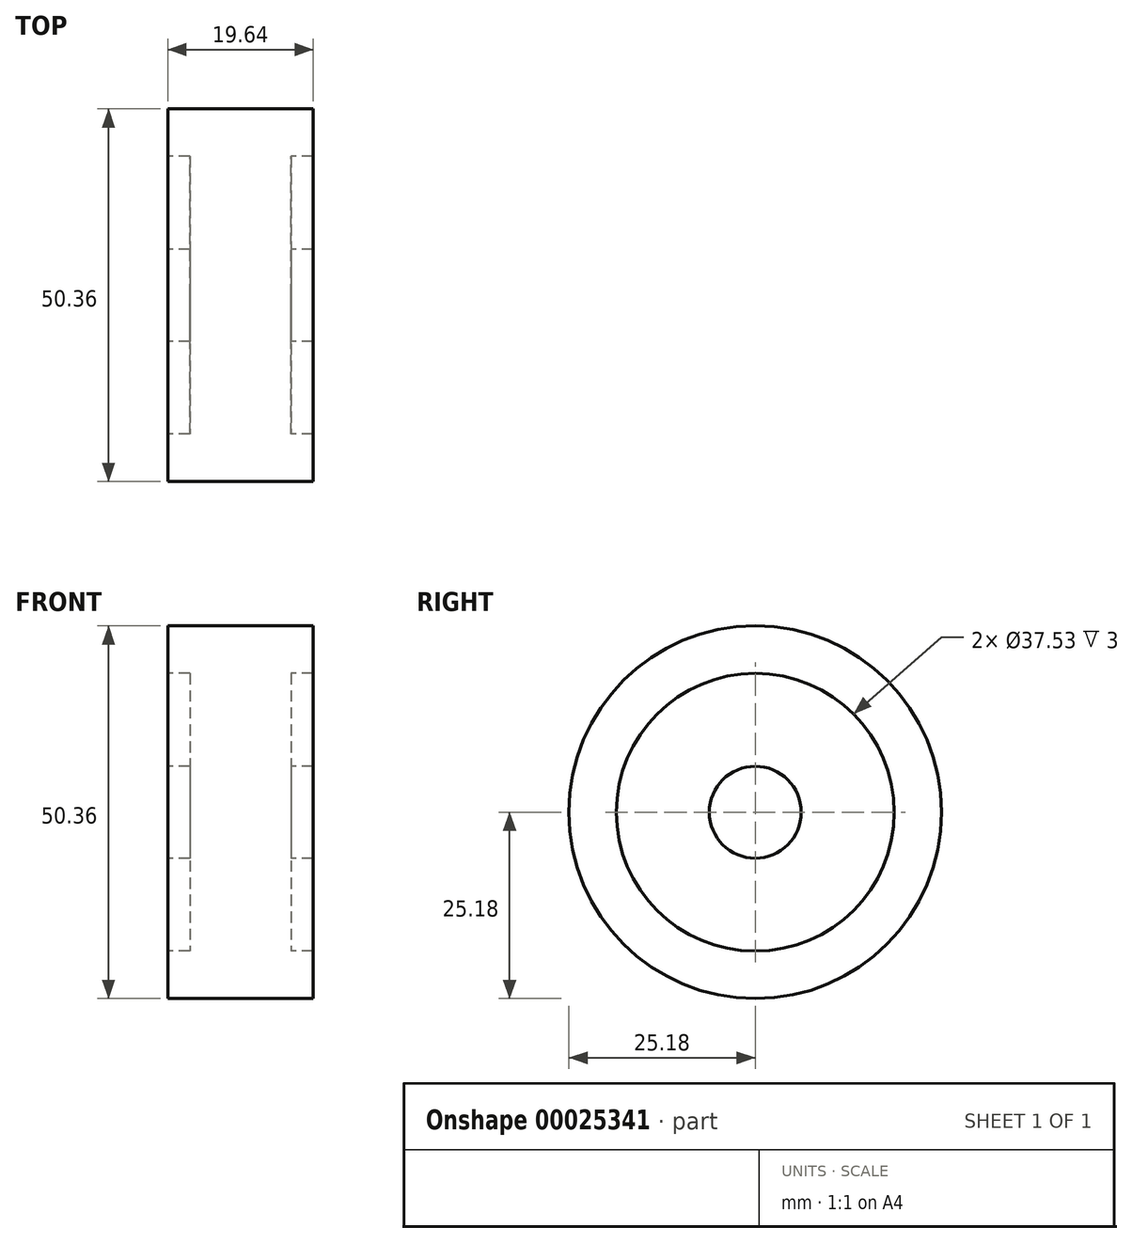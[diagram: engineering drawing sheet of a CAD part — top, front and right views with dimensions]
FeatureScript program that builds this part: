
annotation { "Feature Type Name" : "Feature", "Feature Type Description" : "" }
export const myFeature = defineFeature(function(context is Context, id is Id, definition is map)
    precondition{}
    {
        {
            var Q0;
            Q0=qCreatedBy(makeId("Front.planeOp"),FACE);
            var sketch = newSketch(context, id + "F0", { "sketchPlane" : qUnion([Q0])});
            skLineSegment(sketch, "E0", {"start": v(-18.7, 0) * mm, "end": v(23.1, 0) * mm, "construction": true});
            skLineSegment(sketch, "E1", {"start": v(0, 0) * mm, "end": v(0, 6.21) * mm});
            skLineSegment(sketch, "E2", {"start": v(0, 6.21) * mm, "end": v(-3, 6.21) * mm});
            skLineSegment(sketch, "E3", {"start": v(-3, 6.21) * mm, "end": v(-3, 18.77) * mm});
            skLineSegment(sketch, "E4", {"start": v(-3, 18.77) * mm, "end": v(0, 18.77) * mm});
            skLineSegment(sketch, "E5", {"start": v(0, 18.77) * mm, "end": v(0, 25.18) * mm});
            skLineSegment(sketch, "E6", {"start": v(0, 25.18) * mm, "end": v(-19.64, 25.18) * mm});
            skLineSegment(sketch, "E7", {"start": v(-19.64, 25.18) * mm, "end": v(-19.64, 18.77) * mm});
            skLineSegment(sketch, "E8", {"start": v(-19.64, 18.77) * mm, "end": v(-16.64, 18.77) * mm});
            skLineSegment(sketch, "E9", {"start": v(-16.64, 18.77) * mm, "end": v(-16.64, 6.21) * mm});
            skLineSegment(sketch, "E10", {"start": v(-16.64, 6.21) * mm, "end": v(-19.64, 6.21) * mm});
            skLineSegment(sketch, "E11", {"start": v(-19.64, 6.21) * mm, "end": v(-19.64, 0) * mm});
            skLineSegment(sketch, "E12", {"start": v(-19.64, 0) * mm, "end": v(0, 0) * mm});
            skLineSegment(sketch, "E13", {"start": v(-18.7, 0) * mm, "end": v(-33.4, 0) * mm});
            skSolve(sketch);
        }
        {
            var Q0;
            Q0=makeQuery(id+"F0.imprint","IMPRINT",FACE,{"disambiguationData":[TD([[makeQuery(id+"F0.imprint","IMPRINT",EDGE,{"derivedFrom":sQuery(id+"F0.wireOp",EDGE,"E1")}),1.0]])]});
            var Q1;
            Q1=sQuery(id+"F0.wireOp",EDGE,"E0");
            revolve(context, id + "F1", {"entities" : qUnion([Q0]), "axis" : qUnion([Q1]), "revolveType" : RevolveType.FULL});
        }
    });
